# Revit family: Lighting_Emergency&Security_Luznor_Tabled-flush-mounted_ESP
name_source: partatom
category: Lighting Fixtures
revit_build: Autodesk Revit 2018 (Build: 20190510_1515(x64)
units: mm (PartAtom-declared; Revit-internal decimal feet)

## family parameters
Cut with Voids When Loaded = No
Host = Face
Light Source = No
OmniClass Number = 23.35.47.13
OmniClass Title = Emergency Lighting
Part Type = Normal
Room Calculation Point = No
Round Connector Dimension = Use Diameter
Shared = No

## types (1)
- Tabled (flush mounted)
    Altura = 120 mm  [stored 0.393701 ft]
    Anchura = 280 mm  [stored 0.918635 ft]
    Apparent Load = 0 VA
    BIMobject category = Emergency & Security
    Default Elevation = 1219 mm
    Description = Luminaria de emergencia constituida por múltiples leds de baja potencia y alto rendimiento luminoso. Logra la máxima homogeneidad de luz y evita puntos de luz intensa. Posibilidad de encender o apagar los leds en presencia de red (modo permanente y no permanente). Sistema de conexión mediante preplaca.
 Telemandable Serie prevista de una tableta de LED extraplana IP 44 Envolvente 100% policarbonato con difusor transparente de serie con opción de que sea opal suave u opal fuerte. Tecnología LED Baterías Ni-Cd de alta temperatura Eficiencia energética
    Design country = Spain
    Edition number = 1
    Especificación técnica = Color: Blanco frío (5.000 K) Flujo en emergencia (lm): 110 - 580 Flujo en presencia de red (lm): 110 - 580 Indicador de carga: 1 x LED verde Autonomía (h): 1-2-3 Fuente de alimentación: 110 Vac - 230 Vac - 50/60 Hz Telemandable: Si (TL-300) Índice de protección: IP44 - IK04 Aislamiento eléctrico: Clase II Normativa: Marcado CE (93/68/EEC): 2014/35/UE, 2014/30/UE and 2011/65/UE
    Horas de autonomía = Autonomía : 1 hora
    IFC Classification = Lamp
    Información difusor = El difusor se puede solicitar en 3 acabados diferentes: transparente (paso del 100% de la luz), opal suave (paso del 92% de la luz), u ópalo fuerte (paseo del 72% de la luz)
    Intensidad luminosa = Revisar por favor el link en la descripción técnica para comprobar las diferentes opciones ofrecidas por el fabricante
    Lamp = LED
    Manufacturer = Luznor
    Manufacturer country = Spain
    Manufacturer name = Luznor
    Masterformat 2014 Code = 26 52 00
    Masterformat 2014 Description = Emergency Lighting
    Material carcasa LED = Luznor - Plástico - Blanco
    Material cuerpo = Luznor - Plástico - Blanco
    Material main = Polycarbonate
    Model = Tabled (flush mounted)
    NBS Reference Code = 70-50-74
    NBS Reference Description = Self-Contained Emergency Luminaires
    OmniClass Code = 23-35 47 13
    OmniClass Description = Emergency Lighting
    Product Guid = 8d9c4189-725b-4b8e-9f12-c00180cb8d77
    Product SKU = Tabled
    Product data url = https://bimobject.com
    Product family = Tabled series
    Product group = Tabled
    Product name = Tabled
    Product url = https://www.luznor.com
    Profundidad = 48 mm  [stored 0.15748 ft]
    QR code = https://bimobject.com
    UNSPSC Code = 391117
    URL = https://www.luznor.com
    Uniclass 1.4 Code = JV55
    Uniclass 1.4 Description = Self contained emergency and signage systems
    Uniclass 2.0 Code = PR-70-50-74
    Uniclass 2.0 Description = Self-Contained Emergency Luminaires
    Uniclass 2015 Code = Pr_70_70_48_77
    Uniclass 2015 Name = Self-contained emergency luminaires
    Uniformat II Code = D5020
    Uniformat II Description = Lighting & Branch Wiring
    Visibilidad 2D = Yes
    Visibilidad 3D = Yes

note: [stored X ft] marks values corroborated as IEEE doubles in the binary element streams (Revit-internal decimal feet)

## geometry (parser evidence)
native form markers: Sweep x6
no freeform markers — native parametric forms only
